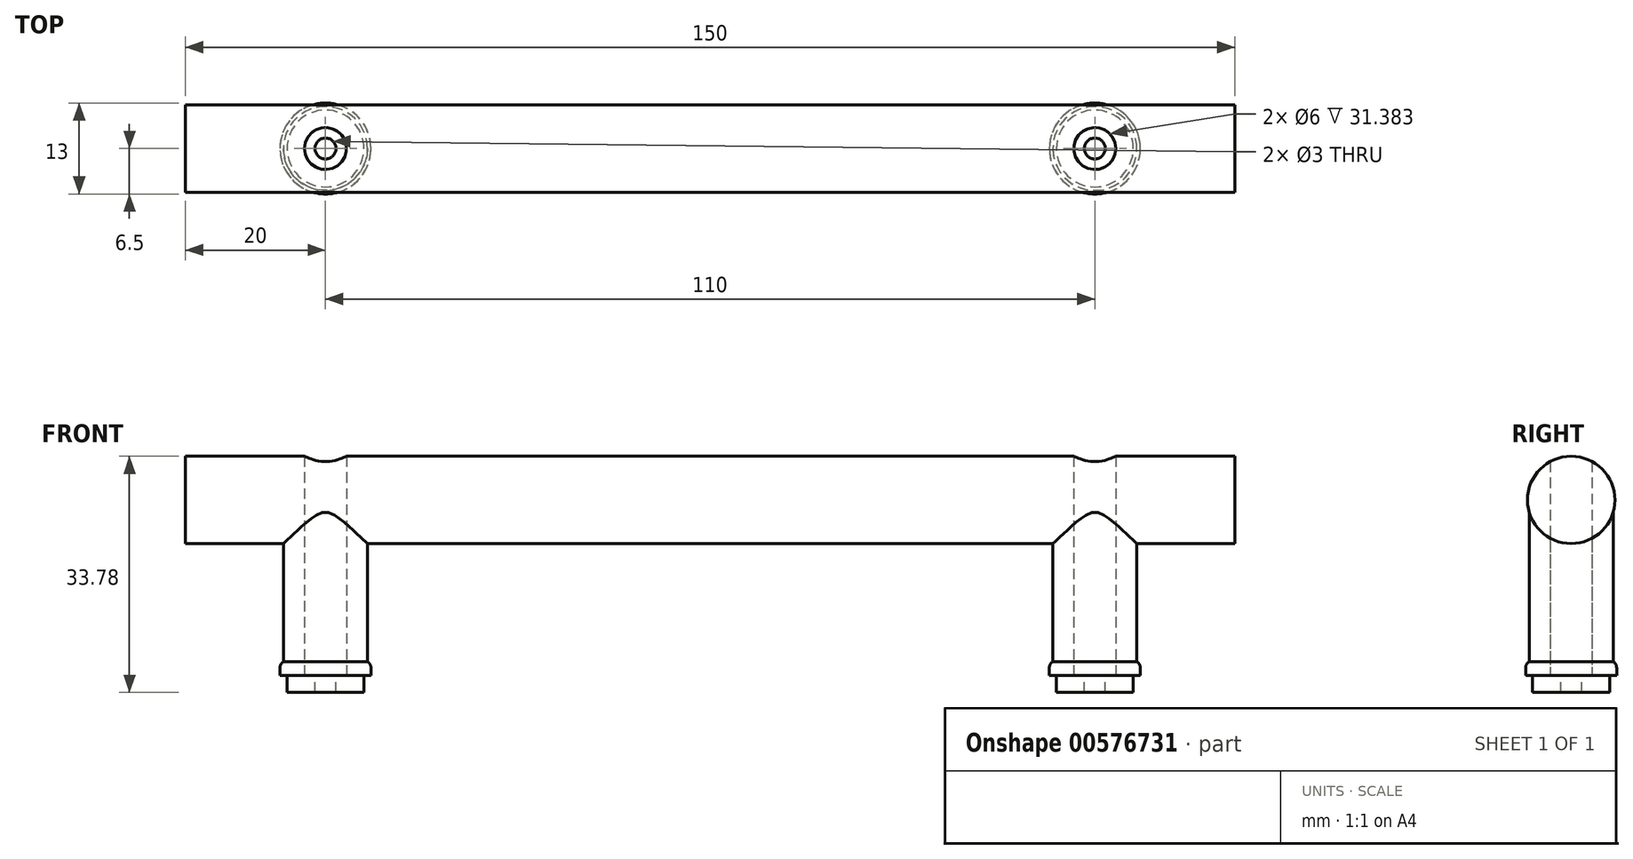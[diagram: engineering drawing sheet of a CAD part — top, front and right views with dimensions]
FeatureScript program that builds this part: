
annotation { "Feature Type Name" : "Feature", "Feature Type Description" : "" }
export const myFeature = defineFeature(function(context is Context, id is Id, definition is map)
    precondition{}
    {
        {
            var Q0;
            Q0=qCreatedBy(makeId("Top.planeOp"),FACE);
            var sketch = newSketch(context, id + "F0", { "sketchPlane" : qUnion([Q0])});
            skCircle(sketch, "E0", {"center": v(-55, 0) * mm, "radius": 6 * mm});
            skCircle(sketch, "E1", {"center": v(-55, 0) * mm, "radius": 5.5 * mm});
            skCircle(sketch, "E2", {"center": v(-55, 0) * mm, "radius": 6.5 * mm});
            skCircle(sketch, "E3", {"center": v(-55, 0) * mm, "radius": 3 * mm});
            skCircle(sketch, "E4", {"center": v(-55, 0) * mm, "radius": 1.5 * mm});
            skSolve(sketch);
        }
        {
            var Q0;
            Q0=makeQuery(id+"F0.imprint","IMPRINT",FACE,{"disambiguationData":[TD([[makeQuery(id+"F0.imprint","IMPRINT",EDGE,{"derivedFrom":sQuery(id+"F0.wireOp",EDGE,"E0")}),1.0]])]});
            var Q1;
            Q1=makeQuery(id+"F0.imprint","IMPRINT",FACE,{"disambiguationData":[TD([[makeQuery(id+"F0.imprint","IMPRINT",EDGE,{"derivedFrom":sQuery(id+"F0.wireOp",EDGE,"E1")}),1.0]])]});
            var Q2;
            Q2=sQuery(id+"F0.wireOp",EDGE,"E0");
            var Q3;
            Q3=sQuery(id+"F0.wireOp",EDGE,"E3");
            extrude(context, id + "F1", {"entities" : qUnion([Q0, Q1]), "surfaceEntities" : qUnion([Q2, Q3]), "depth" : 25 * mm, "offsetDistance" : 25 * mm});
        }
        {
            var Q0;
            Q0=makeQuery(id+"F0.imprint","IMPRINT",FACE,{"disambiguationData":[TD([[makeQuery(id+"F0.imprint","IMPRINT",EDGE,{"derivedFrom":sQuery(id+"F0.wireOp",EDGE,"E0")}),-1.0]])]});
            extrude(context, id + "F2", {"entities" : qUnion([Q0]), "operationType" : NewBodyOperationType.ADD, "depth" : 2 * mm, "offsetDistance" : 25 * mm});
        }
        {
            var Q0;
            Q0=makeQuery(id+"F0.imprint","IMPRINT",FACE,{"disambiguationData":[TD([[makeQuery(id+"F0.imprint","IMPRINT",EDGE,{"derivedFrom":sQuery(id+"F0.wireOp",EDGE,"E1")}),1.0]])]});
            var Q1;
            Q1=makeQuery(id+"F0.imprint","IMPRINT",FACE,{"disambiguationData":[TD([[makeQuery(id+"F0.imprint","IMPRINT",EDGE,{"derivedFrom":sQuery(id+"F0.wireOp",EDGE,"E3")}),1.0]])]});
            extrude(context, id + "F3", {"entities" : qUnion([Q0, Q1]), "operationType" : NewBodyOperationType.ADD, "depth" : -2.4 * mm, "offsetDistance" : 25 * mm});
        }
        {
            var Q0;
            Q0=qCreatedBy(makeId("Right.planeOp"),FACE);
            var sketch = newSketch(context, id + "F4", { "sketchPlane" : qUnion([Q0])});
            skCircle(sketch, "E5", {"center": v(0, 25.13) * mm, "radius": 6.25 * mm});
            skSolve(sketch);
        }
        {
            var Q0;
            Q0=makeQuery(id+"F4.imprint","IMPRINT",FACE,{"disambiguationData":[TD([[makeQuery(id+"F4.imprint","IMPRINT",EDGE,{"derivedFrom":sQuery(id+"F4.wireOp",EDGE,"E5")}),1.0]])]});
            extrude(context, id + "F5", {"entities" : qUnion([Q0]), "operationType" : NewBodyOperationType.ADD, "oppositeDirection" : true, "depth" : 75 * mm, "offsetDistance" : 25 * mm});
        }
        {
            var Q0;
            Q0=makeQuery(id+"F0.imprint","IMPRINT",FACE,{"disambiguationData":[TD([[makeQuery(id+"F0.imprint","IMPRINT",EDGE,{"derivedFrom":sQuery(id+"F0.wireOp",EDGE,"E3")}),1.0]])]});
            var Q1;
            Q1=makeQuery(id+"F0.imprint","IMPRINT",FACE,{"disambiguationData":[TD([[makeQuery(id+"F0.imprint","IMPRINT",EDGE,{"derivedFrom":sQuery(id+"F0.wireOp",EDGE,"E4")}),1.0]])]});
            extrude(context, id + "F6", {"entities" : qUnion([Q0, Q1]), "operationType" : NewBodyOperationType.REMOVE, "depth" : 40 * mm, "offsetDistance" : 25 * mm});
        }
        {
            var Q0;
            Q0=makeQuery(id+"F2.opExtrude","CAP_EDGE",EDGE,{"disambiguationData":[OSD([sQuery(id+"F0.wireOp",EDGE,"E2")])],"isStart":false});
            fillet(context, id + "F7", {"entities" : qUnion([Q0]), "radius" : 1 * mm, "tangentPropagation" : true, "allowEdgeOverflow" : false});
        }
        {
            var Q0;
            Q0=makeQuery(id+"F1.opExtrude","SWEPT_BODY",BODY,{"disambiguationData":[OSD([sQuery(id+"F0.wireOp",EDGE,"E0"),sQuery(id+"F0.wireOp",EDGE,"E3")])]});
            var Q1;
            Q1=qCreatedBy(makeId("Right.planeOp"),FACE);
            mirror(context, id + "F8", {"operationType" : NewBodyOperationType.ADD, "entities" : qUnion([Q0]), "mirrorPlane" : qUnion([Q1])});
        }
    });
